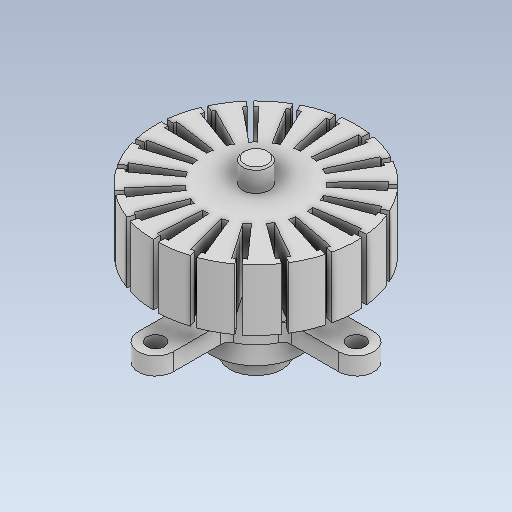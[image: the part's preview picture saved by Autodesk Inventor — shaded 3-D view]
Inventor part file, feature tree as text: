
AUTODESK INVENTOR PART (.ipt)
format: ipt  version: 2020 (Build 240168000, 168)  size: 413,184 bytes
history: native  units: mm
features: sketch x8, other x3, plane x1
ambient origin geometry x8: Origin, YZ Plane, XZ Plane, XY Plane, X Axis, Y Axis, Z Axis, Center Point
bodies: Solid1 (feature_tree)
feature tree (12):
  other  "mot_27_2.ipt"
  other  "Solid1::mot_27_2.ipt"
  other  "TaggingFeature1"
  sketch  "Sketch1"  dims[d0=10.0mm]
  sketch  "Sketch2"
  sketch  "Sketch3"
  sketch  "Sketch4"
  sketch  "Sketch5"
  sketch  "Sketch6"
  sketch  "Sketch7"
  sketch  "Sketch8"
  plane  "Work Plane1"
